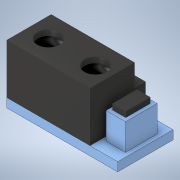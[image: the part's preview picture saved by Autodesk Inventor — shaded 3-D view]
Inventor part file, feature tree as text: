
AUTODESK INVENTOR PART (.ipt)
format: ipt  version: 2020 (Build 240168000, 168)  size: 210,432 bytes
history: native  units: mm
features: sketch x7, extrude x6, plane x4, other x1
ambient origin geometry x8: Origin, YZ Plane, XZ Plane, XY Plane, X Axis, Y Axis, Z Axis, Center Point
bodies: Solid2 (feature_tree)
feature tree (18):
  other  "Bryła1"
  extrude  "Wyciągnięcie proste1"  Depth=15.0mm
  extrude  "Wyciągnięcie proste2"  Depth=5.0mm
  extrude  "Wyciągnięcie proste3"  Depth=8.0mm
  extrude  "Extrusion4"  Depth=4.0mm
  extrude  "Extrusion5"  Depth=3.5mm
  extrude  "Extrusion7"  Depth=4.0mm
  plane  "Work Plane1"
  plane  "Work Plane2"
  plane  "Work Plane3"
  plane  "Work Plane4"
  sketch  "Sketch9"  dims[d7=4.0mm d8=0.0mm d9=4.0mm d10=3.5mm d11=4.0mm d12=3.0mm d13=4.0mm d14=4.0mm d15=1.0mm d16=0.0mm d17=1.6mm d18=0.0mm d19=20.0mm d20=3.5mm d21=5.7mm d22=2.15mm d23=0.75mm d24=4.8mm d25=0.0mm d32=4.4mm d33=0.65mm d34=2.4mm d35=0.5mm d36=1.0mm d37=0.0mm d38=-2.0mm d45=-1.0mm d46=-1.0mm d47=0.4mm d48=0.0mm d49=1.0mm d50=3.054326mm d51=6.108652mm d53=3.0mm d86=-5.0mm d54=0.872665mm d55=0.872665mm d83=0.5mm d84=0.872665mm d85=0.5mm d87=0.872665mm d88=0.5mm d89=0.872665mm]
  sketch  "Szkic1"
  sketch  "Szkic2"
  sketch  "Szkic3"
  sketch  "Sketch4"  dims[d0=10.0mm d1=15.0mm]
  sketch  "Sketch5"  dims[d2=5.0mm d3=7.5mm]
  sketch  "Sketch7"  dims[d4=5.0mm d5=0.0mm d6=8.0mm]
